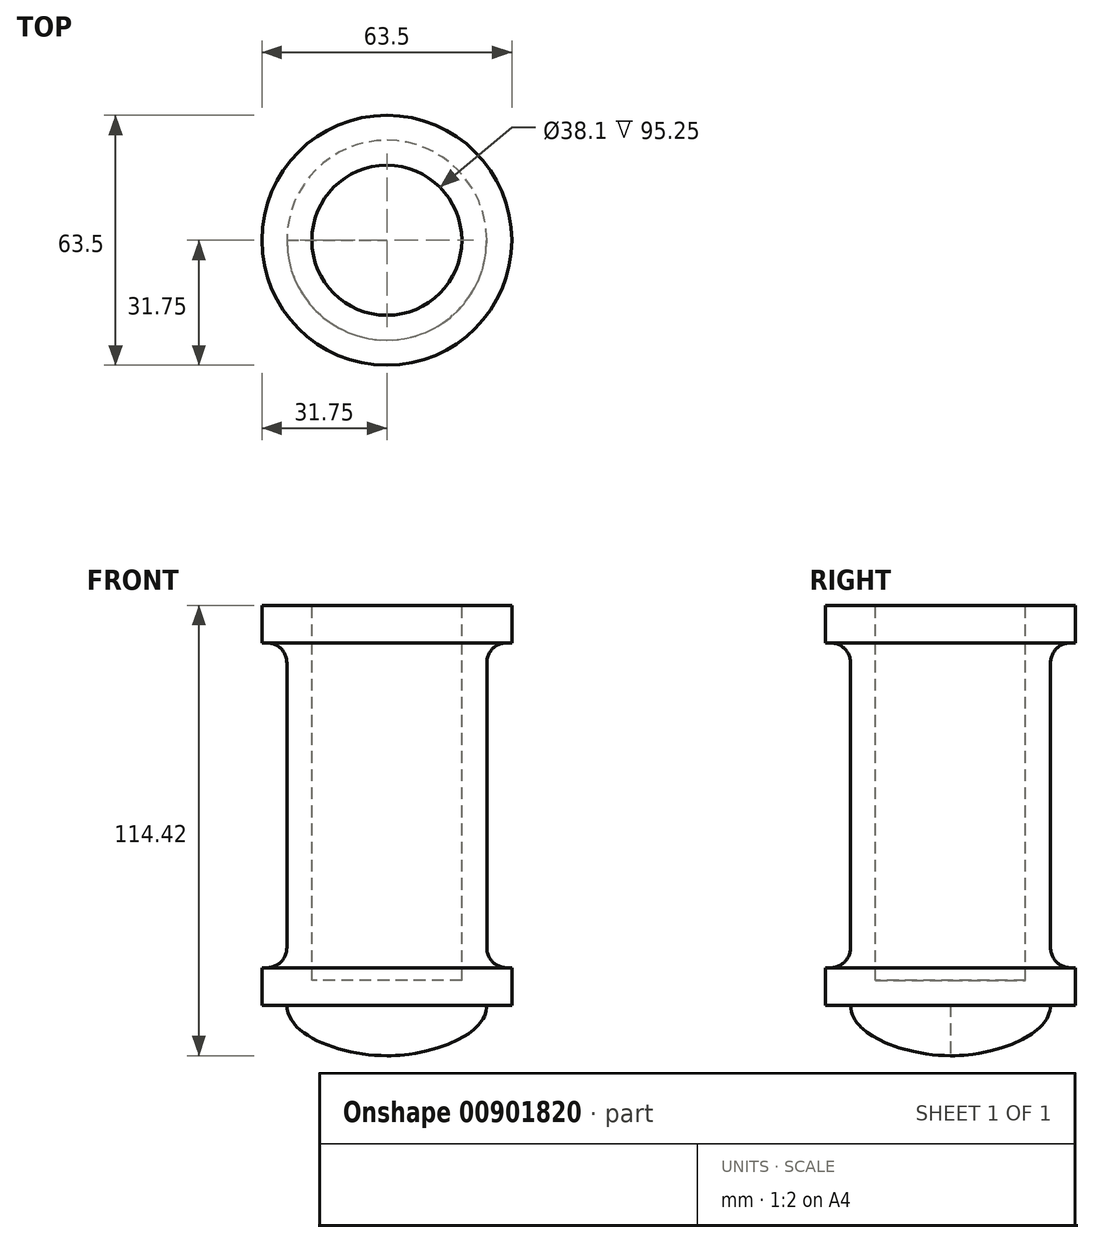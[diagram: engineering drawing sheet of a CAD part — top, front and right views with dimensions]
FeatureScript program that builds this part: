
annotation { "Feature Type Name" : "Feature", "Feature Type Description" : "" }
export const myFeature = defineFeature(function(context is Context, id is Id, definition is map)
    precondition{}
    {
        {
            var Q0;
            Q0=qCreatedBy(makeId("Top.planeOp"),FACE);
            var sketch = newSketch(context, id + "F0", { "sketchPlane" : qUnion([Q0])});
            skCircle(sketch, "E0", {"center": v(0, 0) * mm, "radius": 25.4 * mm});
            skSolve(sketch);
        }
        {
            var Q0;
            Q0=makeQuery(id+"F0.imprint","IMPRINT",FACE,{"disambiguationData":[TD([[makeQuery(id+"F0.imprint","IMPRINT",EDGE,{"derivedFrom":sQuery(id+"F0.wireOp",EDGE,"E0")}),1.0]])]});
            var Q1;
            Q1=sQuery(id+"F0.wireOp",EDGE,"E0");
            extrude(context, id + "F1", {"entities" : qUnion([Q0]), "surfaceEntities" : qUnion([Q1]), "depth" : 101.6 * mm, "offsetDistance" : 25.4 * mm});
        }
        {
            var Q0;
            Q0=qCreatedBy(makeId("Front.planeOp"),FACE);
            var sketch = newSketch(context, id + "F2", { "sketchPlane" : qUnion([Q0])});
            skLineSegment(sketch, "E1", {"start": v(0, 0) * mm, "end": v(0, -12.82) * mm});
            skFitSpline(sketch, "E2", {"points": [v(-25.4, 0) * mm, v(0, -12.82) * mm], "startDerivative": vector(0, -23.13) * mm, "endDerivative": vector(34.82, 0) * mm});
            skLineSegment(sketch, "E3", {"start": v(-25.4, 0) * mm, "end": v(-25.4, 101.6) * mm, "construction": true});
            skLineSegment(sketch, "E4", {"start": v(-25.4, 0) * mm, "end": v(0, 0) * mm});
            skSolve(sketch);
        }
        {
            var Q0;
            Q0=makeQuery(id+"F2.imprint","IMPRINT",FACE,{"disambiguationData":[TD([[makeQuery(id+"F2.imprint","IMPRINT",EDGE,{"derivedFrom":sQuery(id+"F2.wireOp",EDGE,"E1")}),-1.0]])]});
            var Q1;
            Q1=sQuery(id+"F2.wireOp",EDGE,"E1");
            revolve(context, id + "F3", {"operationType" : NewBodyOperationType.ADD, "surfaceOperationType" : NewSurfaceOperationType.NEW, "entities" : qUnion([Q0]), "axis" : qUnion([Q1]), "revolveType" : RevolveType.FULL});
        }
        {
            var Q0;
            Q0=qCreatedBy(makeId("Front.planeOp"),FACE);
            var sketch = newSketch(context, id + "F4", { "sketchPlane" : qUnion([Q0])});
            skLineSegment(sketch, "E5", {"start": v(0, 0) * mm, "end": v(0, 9.53) * mm});
            skLineSegment(sketch, "E6", {"start": v(0, 9.53) * mm, "end": v(31.75, 9.53) * mm});
            skLineSegment(sketch, "E7", {"start": v(31.75, 9.53) * mm, "end": v(31.75, 0) * mm});
            skLineSegment(sketch, "E8", {"start": v(31.75, 0) * mm, "end": v(0, 0) * mm});
            skPoint(sketch, "E9", {"position": v(25.4, 9.53) * mm});
            skPoint(sketch, "E10", {"position": v(25.4, 0) * mm});
            skLineSegment(sketch, "E11", {"start": v(0, 9.53) * mm, "end": v(0, 92.08) * mm});
            skLineSegment(sketch, "E12", {"start": v(0, 92.08) * mm, "end": v(0, 101.6) * mm});
            skLineSegment(sketch, "E13", {"start": v(0, 101.6) * mm, "end": v(31.75, 101.6) * mm});
            skLineSegment(sketch, "E14", {"start": v(31.75, 101.6) * mm, "end": v(31.75, 92.08) * mm});
            skLineSegment(sketch, "E15", {"start": v(31.75, 92.08) * mm, "end": v(0, 92.08) * mm});
            skSolve(sketch);
        }
        {
            var Q0;
            Q0=makeQuery(id+"F4.imprint","IMPRINT",FACE,{"disambiguationData":[TD([[makeQuery(id+"F4.imprint","IMPRINT",EDGE,{"derivedFrom":sQuery(id+"F4.wireOp",EDGE,"E5")}),-1.0]])]});
            var Q1;
            Q1=makeQuery(id+"F4.imprint","IMPRINT",FACE,{"disambiguationData":[TD([[makeQuery(id+"F4.imprint","IMPRINT",EDGE,{"derivedFrom":sQuery(id+"F4.wireOp",EDGE,"E12")}),-1.0]])]});
            var Q2;
            Q2=sQuery(id+"F4.wireOp",EDGE,"E5");
            revolve(context, id + "F5", {"operationType" : NewBodyOperationType.ADD, "surfaceOperationType" : NewSurfaceOperationType.NEW, "entities" : qUnion([Q0, Q1]), "axis" : qUnion([Q2]), "revolveType" : RevolveType.FULL});
        }
        {
            var Q0;
            Q0=makeQuery(id+"F5.boolean.opBoolean","INTERSECT",EDGE,{"derivedFrom":[makeQuery(id+"F1.opExtrude","SWEPT_FACE",FACE,{"disambiguationData":[OSD([sQuery(id+"F0.wireOp",EDGE,"E0")])]}),makeQuery(id+"F5.opRevolve","SWEPT_FACE",FACE,{"disambiguationData":[OSD([sQuery(id+"F4.wireOp",EDGE,"E15")])]})]});
            var Q1;
            Q1=makeQuery(id+"F5.boolean.opBoolean","INTERSECT",EDGE,{"derivedFrom":[makeQuery(id+"F1.opExtrude","SWEPT_FACE",FACE,{"disambiguationData":[OSD([sQuery(id+"F0.wireOp",EDGE,"E0")])]}),makeQuery(id+"F5.opRevolve","SWEPT_FACE",FACE,{"disambiguationData":[OSD([sQuery(id+"F4.wireOp",EDGE,"E6")])]})]});
            fillet(context, id + "F6", {"entities" : qUnion([Q0, Q1]), "radius" : 5.08 * mm, "tangentPropagation" : true, "allowEdgeOverflow" : false});
        }
        {
            var Q0;
            Q0=makeQuery(id+"F5.boolean.opBoolean","MERGE",FACE,{"derivedFrom":[makeQuery(id+"F1.opExtrude","CAP_FACE",FACE,{"disambiguationData":[OSD([sQuery(id+"F0.wireOp",EDGE,"E0")])],"isStart":false}),makeQuery(id+"F5.opRevolve","SWEPT_FACE",FACE,{"disambiguationData":[OSD([sQuery(id+"F4.wireOp",EDGE,"E13")])]})]});
            var sketch = newSketch(context, id + "F7", { "sketchPlane" : qUnion([Q0])});
            skCircle(sketch, "E16", {"center": v(0, 0) * mm, "radius": 19.05 * mm});
            skSolve(sketch);
        }
        {
            var Q0;
            Q0=makeQuery(id+"F7.imprint","IMPRINT",FACE,{"disambiguationData":[TD([[makeQuery(id+"F7.imprint","IMPRINT",EDGE,{"derivedFrom":sQuery(id+"F7.wireOp",EDGE,"E16")}),1.0]])]});
            var Q1;
            Q1=sQuery(id+"F7.wireOp",EDGE,"E16");
            extrude(context, id + "F8", {"entities" : qUnion([Q0]), "operationType" : NewBodyOperationType.REMOVE, "surfaceEntities" : qUnion([Q1]), "oppositeDirection" : true, "depth" : 95.25 * mm, "offsetDistance" : 25.4 * mm});
        }
    });
